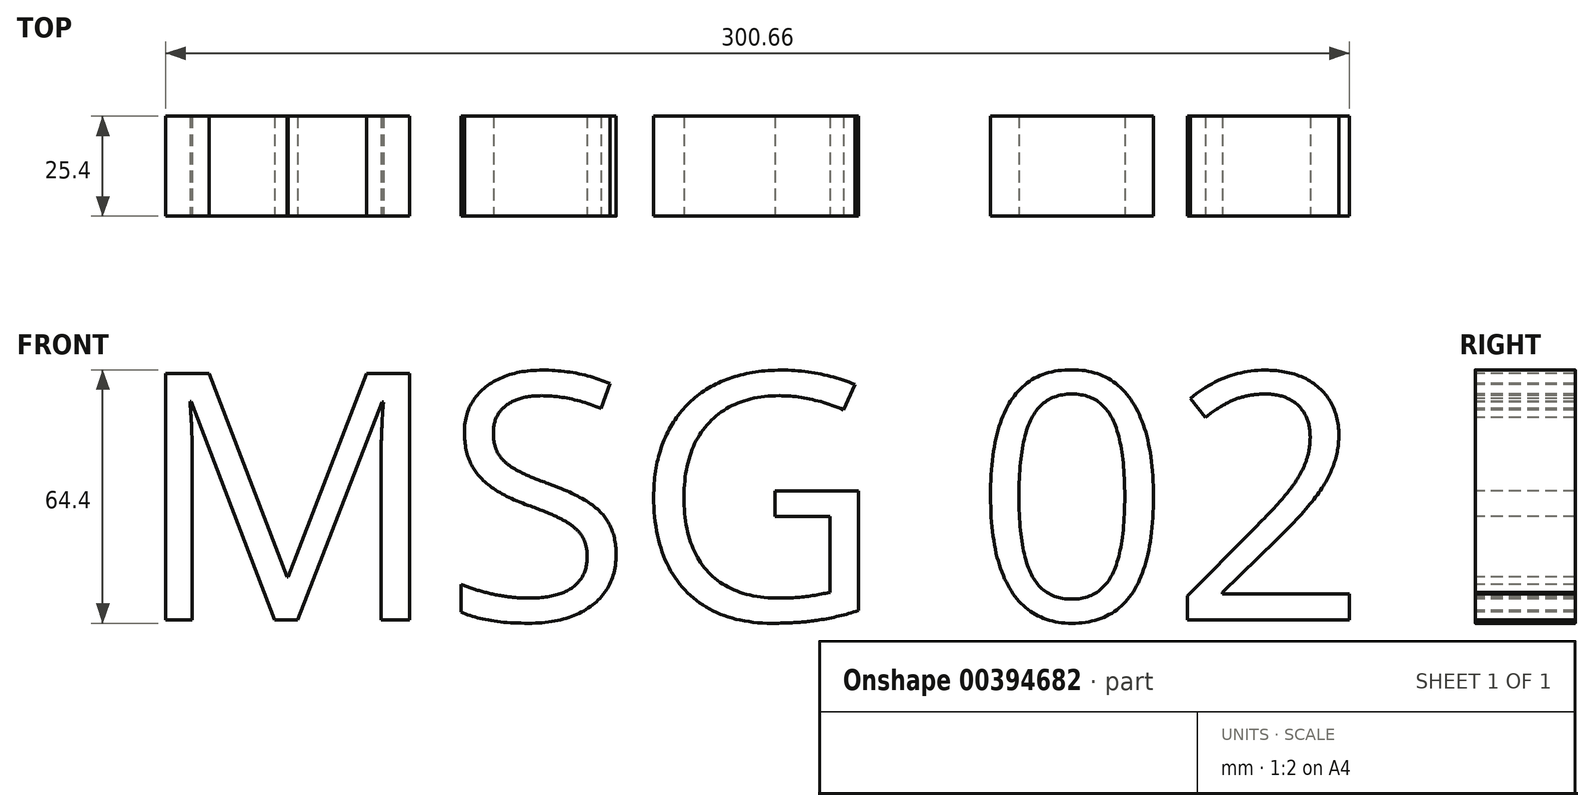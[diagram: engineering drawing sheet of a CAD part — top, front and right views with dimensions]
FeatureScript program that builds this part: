
annotation { "Feature Type Name" : "Feature", "Feature Type Description" : "" }
export const myFeature = defineFeature(function(context is Context, id is Id, definition is map)
    precondition{}
    {
        {
            var Q0;
            Q0=qCreatedBy(makeId("Front.planeOp"),FACE);
            var sketch = newSketch(context, id + "F0", { "sketchPlane" : qUnion([Q0])});
            skText(sketch, "E0", { "text": "MSG 02", "fontName": "OpenSans-Regular.ttf"});
            const initialGuessF0  = {"E0": [-0.17296, -0.02315, 1, 0, 0.06309]};
            skSetInitialGuess(sketch, initialGuessF0);
            skSolve(sketch);
        }
        {
            var Q0;
            Q0 = qConstructionFilter(qBodyType(qCreatedBy(id + "F0" ,EDGE), BodyType.WIRE), ConstructionObject.NO);
            extrude(context, id + "F1", {"bodyType" : ToolBodyType.SURFACE, "surfaceEntities" : qUnion([Q0]), "depth" : 25.4 * mm});
        }
    });
